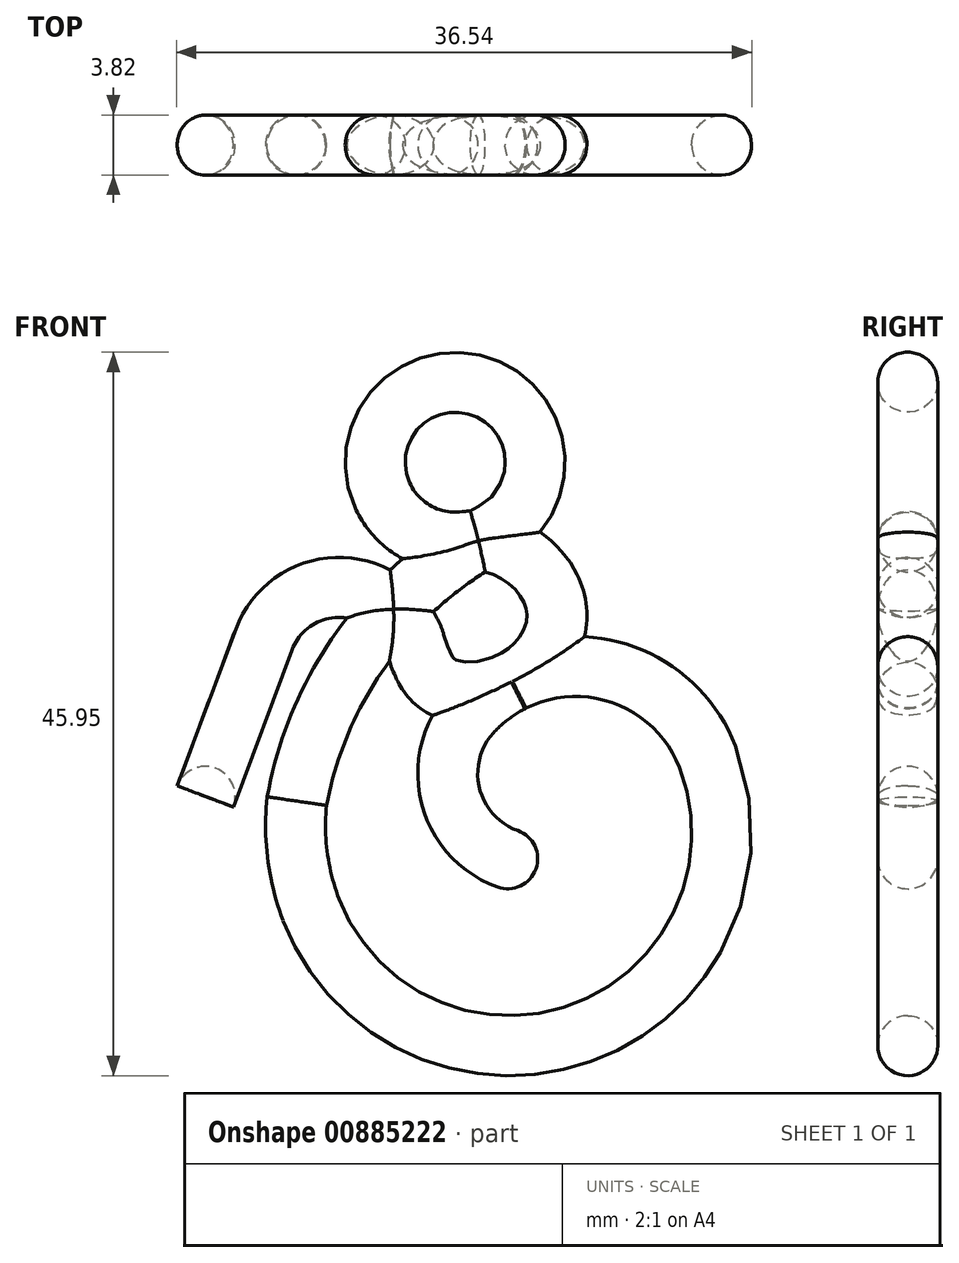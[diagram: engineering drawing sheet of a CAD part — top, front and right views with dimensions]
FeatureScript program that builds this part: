
annotation { "Feature Type Name" : "Feature", "Feature Type Description" : "" }
export const myFeature = defineFeature(function(context is Context, id is Id, definition is map)
    precondition{}
    {
        {
            var Q0;
            Q0=qCreatedBy(makeId("Front.planeOp"),FACE);
            var sketch = newSketch(context, id + "F0", { "sketchPlane" : qUnion([Q0])});
            skArc(sketch, "E0", {"start": v(4.95, 21.27) * mm, "mid": v(-3.22, 14.16) * mm, "end": v(-7.5, 4.22) * mm});
            skArc(sketch, "E1", {"start": v(18.56, 7.04) * mm, "mid": v(11.85, 12.62) * mm, "end": v(3.57, 9.84) * mm});
            skArc(sketch, "E2", {"start": v(3.57, 9.84) * mm, "mid": v(2.24, 4.58) * mm, "end": v(5.88, 0.55) * mm});
            skLineSegment(sketch, "E3", {"start": v(5.88, 0.55) * mm, "end": v(3.54, -5.9) * mm, "construction": true});
            skArc(sketch, "E4", {"start": v(-7.5, 4.22) * mm, "mid": v(-7.47, 0.71) * mm, "end": v(-6.6, -2.69) * mm});
            skArc(sketch, "E5", {"start": v(-6.6, -2.69) * mm, "mid": v(10.85, -10.4) * mm, "end": v(18.56, 7.04) * mm});
            skArc(sketch, "E6", {"start": v(0, 14.25) * mm, "mid": v(-4.72, 17.8) * mm, "end": v(-9.6, 14.49) * mm});
            skLineSegment(sketch, "E7", {"start": v(-9.6, 14.49) * mm, "end": v(-13.33, 4.52) * mm});
            skCircle(sketch, "E8", {"center": v(2.55, 25.75) * mm, "radius": 3.18 * mm, "construction": true});
            skCircle(sketch, "E9", {"center": v(3.88, 15.67) * mm, "radius": 3.18 * mm, "construction": true});
            skLineSegment(sketch, "E10", {"start": v(2.55, 25.75) * mm, "end": v(3.88, 15.67) * mm, "construction": true});
            skLineSegment(sketch, "E11", {"start": v(2.55, 25.75) * mm, "end": v(5.88, 0.55) * mm, "construction": true});
            skArc(sketch, "E12.0", {"start": v(4.95, 21.27) * mm, "mid": v(4.2, 30.55) * mm, "end": v(-2.09, 23.67) * mm});
            skCircle(sketch, "E13", {"center": v(3.88, 15.67) * mm, "radius": 5.08 * mm, "construction": true});
            skFitSpline(sketch, "E14", {"points": [v(3.22, 20.71) * mm, v(7.83, 18.87) * mm, v(8.94, 15.25) * mm, v(6.1, 11.78) * mm, v(1.62, 11.55) * mm, v(0, 14.25) * mm], "startDerivative": vector(24.6, 3.25) * mm, "endDerivative": vector(-6.02, 18.96) * mm});
            skArc(sketch, "E15", {"start": v(-2.09, 23.67) * mm, "mid": v(0.07, 21.31) * mm, "end": v(3.22, 20.71) * mm});
            skSolve(sketch);
        }
        {
            var Q0;
            Q0=sQuery(id+"F0.wireOp",EDGE,"E3");
            cPlane(context, id + "F1", {"entities" : qUnion([Q0]), "cplaneType" : CPlaneType.LINE_ANGLE, "offset" : 25.4 * mm, "angle" : 0 * degree, "width" : 152.4 * mm, "height" : 152.4 * mm});
        }
        {
            var Q0;
            Q0=qCreatedBy(id+"F1.planeOp",FACE);
            var sketch = newSketch(context, id + "F2", { "sketchPlane" : qUnion([Q0])});
            skPoint(sketch, "E16.0", {"position": v(0, 2.53) * mm});
            skCircle(sketch, "E17", {"center": v(0, 2.53) * mm, "radius": 1.9 * mm});
            skLineSegment(sketch, "E18", {"start": v(0, 0.62) * mm, "end": v(0, 4.43) * mm});
            skSolve(sketch);
        }
        {
            var Q0;
            Q0=makeQuery(id+"F2.imprint","IMPRINT",FACE,{"disambiguationData":[TD([[makeQuery(id+"F2.imprint","IMPRINT",EDGE,{"derivedFrom":sQuery(id+"F2.wireOp",EDGE,"E17")}),1.0]])]});
            var Q1;
            Q1=sQuery(id+"F0.wireOp",EDGE,"E2");
            var Q2;
            Q2=sQuery(id+"F0.wireOp",EDGE,"E1");
            var Q3;
            Q3=sQuery(id+"F0.wireOp",EDGE,"E5");
            var Q4;
            Q4=sQuery(id+"F0.wireOp",EDGE,"E4");
            var Q5;
            Q5=sQuery(id+"F0.wireOp",EDGE,"E0");
            var Q6;
            Q6=sQuery(id+"F0.wireOp",EDGE,"E12.0");
            sweep(context, id + "F3", {"profiles" : qUnion([Q0]), "path" : qUnion([Q1, Q2, Q3, Q4, Q5, Q6])});
        }
        {
            var Q0;
            Q0=makeQuery(id+"F3.opSweep","CAP_FACE",FACE,{"disambiguationData":[OSD([sQuery(id+"F0.wireOp",VERTEX,"5kSYbBWt-iHNA-QvRj-P9VA-2Qk3GOujtevp.end"),sQuery(id+"F2.wireOp",EDGE,"E17")])],"isStart":false});
            var Q1;
            Q1=sQuery(id+"F0.wireOp",EDGE,"E15");
            var Q2;
            Q2=sQuery(id+"F0.wireOp",EDGE,"E14");
            var Q3;
            Q3=sQuery(id+"F0.wireOp",EDGE,"E6");
            var Q4;
            Q4=sQuery(id+"F0.wireOp",EDGE,"E7");
            sweep(context, id + "F4", {"operationType" : NewBodyOperationType.ADD, "profiles" : qUnion([Q0]), "path" : qUnion([Q1, Q2, Q3, Q4])});
        }
        {
            var Q0;
            {var subQ0=sQuery(id+"F2.wireOp",EDGE,"E18");Q0=makeQuery(id+"F2.imprint","IMPRINT",FACE,{"disambiguationData":[TD([[makeQuery(id+"F2.imprint","IMPRINT",EDGE,{"derivedFrom":subQ0}),1.0]])]});}
            var Q1;
            Q1=sQuery(id+"F2.wireOp",EDGE,"E18");
            revolve(context, id + "F5", {"operationType" : NewBodyOperationType.ADD, "surfaceOperationType" : NewSurfaceOperationType.NEW, "entities" : qUnion([Q0]), "axis" : qUnion([Q1]), "revolveType" : RevolveType.ONE_DIRECTION, "oppositeDirection" : true, "angle" : 180 * degree});
        }
        {
            var Q0;
            Q0=makeQuery(id+"F4.opSweep","CAP_FACE",FACE,{"disambiguationData":[OSD([sQuery(id+"F0.wireOp",VERTEX,"5kSYbBWt-iHNA-QvRj-P9VA-2Qk3GOujtevp.end"),sQuery(id+"F0.wireOp",VERTEX,"z1g85lVo-6ld4-QNVT-E2m7-ixDHGi65ZvCZ.end"),sQuery(id+"F2.wireOp",EDGE,"E17")])],"isStart":false});
            var sketch = newSketch(context, id + "F6", { "sketchPlane" : qUnion([Q0])});
            skCircle(sketch, "E19.0.0", {"center": v(-14.06, 0) * mm, "radius": 1.9 * mm});
            skLineSegment(sketch, "E20", {"start": v(-14.44, -1.87) * mm, "end": v(-13.68, 1.87) * mm});
            skSolve(sketch);
        }
        {
            var Q0;
            {var subQ0=sQuery(id+"F6.wireOp",EDGE,"E20");Q0=makeQuery(id+"F6.imprint","IMPRINT",FACE,{"disambiguationData":[TD([[makeQuery(id+"F6.imprint","IMPRINT",EDGE,{"derivedFrom":subQ0}),-1.0]])]});}
            var Q1;
            Q1=sQuery(id+"F6.wireOp",EDGE,"E20");
            revolve(context, id + "F7", {"operationType" : NewBodyOperationType.ADD, "surfaceOperationType" : NewSurfaceOperationType.NEW, "entities" : qUnion([Q0]), "axis" : qUnion([Q1]), "revolveType" : RevolveType.ONE_DIRECTION, "oppositeDirection" : true, "angle" : 180 * degree});
        }
    });
